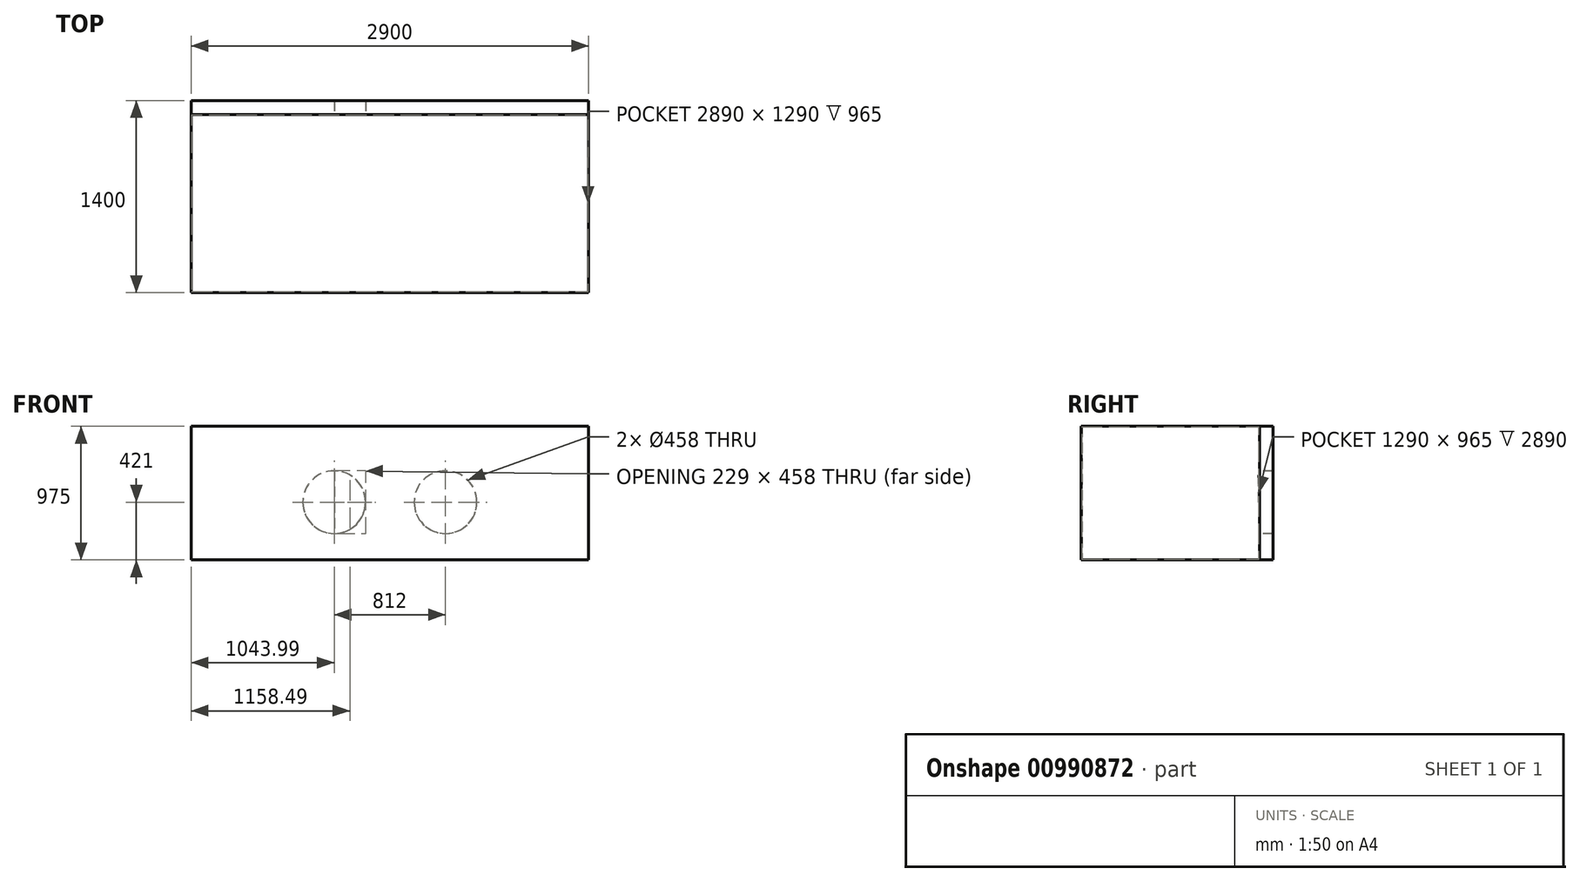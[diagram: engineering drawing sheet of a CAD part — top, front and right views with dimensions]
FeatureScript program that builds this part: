
annotation { "Feature Type Name" : "Feature", "Feature Type Description" : "" }
export const myFeature = defineFeature(function(context is Context, id is Id, definition is map)
    precondition{}
    {
        {
            var Q0;
            Q0=qCreatedBy(makeId("Top.planeOp"),FACE);
            var sketch = newSketch(context, id + "F0", { "sketchPlane" : qUnion([Q0])});
            skLineSegment(sketch, "E0", {"start": v(-44.36, 1284.12) * mm, "end": v(-44.36, -15.88) * mm});
            skLineSegment(sketch, "E1", {"start": v(-44.36, -15.88) * mm, "end": v(2855.64, -15.88) * mm});
            skLineSegment(sketch, "E2", {"start": v(2855.64, -15.88) * mm, "end": v(2855.64, 1284.12) * mm});
            skLineSegment(sketch, "E3", {"start": v(2855.64, 1284.12) * mm, "end": v(-44.36, 1284.12) * mm});
            skSolve(sketch);
        }
        {
            var Q0;
            Q0=makeQuery(id+"F0.imprint","IMPRINT",FACE,{"disambiguationData":[TD([[makeQuery(id+"F0.imprint","IMPRINT",EDGE,{"derivedFrom":sQuery(id+"F0.wireOp",EDGE,"E0")}),1.0]])]});
            extrude(context, id + "F1", {"entities" : qUnion([Q0]), "depth" : 975 * mm, "offsetDistance" : 25 * mm});
        }
        {
            var Q0;
            Q0=makeQuery(id+"F1.opExtrude","SWEPT_FACE",FACE,{"disambiguationData":[OSD([sQuery(id+"F0.wireOp",EDGE,"E3")])]});
            var Q1;
            Q1=makeQuery(id+"F1.opExtrude","SWEPT_BODY",BODY,{"disambiguationData":[OSD([sQuery(id+"F0.wireOp",EDGE,"E0"),sQuery(id+"F0.wireOp",EDGE,"E1"),sQuery(id+"F0.wireOp",EDGE,"E2"),sQuery(id+"F0.wireOp",EDGE,"E3")])]});
            shell(context, id + "F2", {"isHollow" : true, "entities" : qUnion([Q0]), "parts" : qUnion([Q1]), "thickness" : 5 * mm});
        }
        {
            var Q0;
            Q0=makeQuery(id+"F1.opExtrude","SWEPT_FACE",FACE,{"disambiguationData":[OSD([sQuery(id+"F0.wireOp",EDGE,"E3")])]});
            var sketch = newSketch(context, id + "F3", { "sketchPlane" : qUnion([Q0])});
            skLineSegment(sketch, "E4.0", {"start": v(-2855.64, 421) * mm, "end": v(44.36, 421) * mm});
            skLineSegment(sketch, "E5.0", {"start": v(-1811.64, 144.5) * mm, "end": v(-1811.64, 832.46) * mm});
            skLineSegment(sketch, "E6.0", {"start": v(-999.64, 910.53) * mm, "end": v(-999.64, 120.1) * mm});
            skCircle(sketch, "E7", {"center": v(-1811.64, 421) * mm, "radius": 229 * mm});
            skCircle(sketch, "E8", {"center": v(-999.64, 421) * mm, "radius": 229 * mm});
            skSolve(sketch);
        }
        {
            var Q0;
            {var subQ0=sQuery(id+"F3.wireOp",EDGE,"E7");var subQ1=sQuery(id+"F3.wireOp",EDGE,"E4.0");var subQ2=makeQuery(id+"F3.imprint","INTERSECT",VERTEX,{"disambiguationData":[OD(0.0)],"derivedFrom":[subQ1,subQ0]});Q0=makeQuery(id+"F3.imprint","IMPRINT",FACE,{"disambiguationData":[TD([[makeQuery(id+"F3.imprint","IMPRINT",EDGE,{"disambiguationData":[TD([[subQ2,-1.0]])],"derivedFrom":subQ1}),-1.0]])]});}
            var Q1;
            {var subQ0=sQuery(id+"F3.wireOp",EDGE,"E7");var subQ1=sQuery(id+"F3.wireOp",EDGE,"E4.0");var subQ2=makeQuery(id+"F3.imprint","INTERSECT",VERTEX,{"disambiguationData":[OD(0.0)],"derivedFrom":[subQ1,subQ0]});Q1=makeQuery(id+"F3.imprint","IMPRINT",FACE,{"disambiguationData":[TD([[makeQuery(id+"F3.imprint","IMPRINT",EDGE,{"disambiguationData":[TD([[subQ2,-1.0]])],"derivedFrom":subQ1}),1.0]])]});}
            var Q2;
            {var subQ0=sQuery(id+"F3.wireOp",EDGE,"E5.0");var subQ1=sQuery(id+"F3.wireOp",EDGE,"E4.0");var subQ2=makeQuery(id+"F3.imprint","INTERSECT",VERTEX,{"derivedFrom":[subQ1,subQ0]});Q2=makeQuery(id+"F3.imprint","IMPRINT",FACE,{"disambiguationData":[TD([[makeQuery(id+"F3.imprint","IMPRINT",EDGE,{"disambiguationData":[TD([[subQ2,-1.0]])],"derivedFrom":subQ1}),1.0]])]});}
            var Q3;
            {var subQ0=sQuery(id+"F3.wireOp",EDGE,"E5.0");var subQ1=sQuery(id+"F3.wireOp",EDGE,"E4.0");var subQ2=makeQuery(id+"F3.imprint","INTERSECT",VERTEX,{"derivedFrom":[subQ1,subQ0]});Q3=makeQuery(id+"F3.imprint","IMPRINT",FACE,{"disambiguationData":[TD([[makeQuery(id+"F3.imprint","IMPRINT",EDGE,{"disambiguationData":[TD([[subQ2,-1.0]])],"derivedFrom":subQ1}),-1.0]])]});}
            var Q4;
            {var subQ0=sQuery(id+"F3.wireOp",EDGE,"E8");var subQ1=sQuery(id+"F3.wireOp",EDGE,"E4.0");var subQ2=makeQuery(id+"F3.imprint","INTERSECT",VERTEX,{"disambiguationData":[OD(0.0)],"derivedFrom":[subQ1,subQ0]});Q4=makeQuery(id+"F3.imprint","IMPRINT",FACE,{"disambiguationData":[TD([[makeQuery(id+"F3.imprint","IMPRINT",EDGE,{"disambiguationData":[TD([[subQ2,-1.0]])],"derivedFrom":subQ1}),-1.0]])]});}
            var Q5;
            {var subQ0=sQuery(id+"F3.wireOp",EDGE,"E8");var subQ1=sQuery(id+"F3.wireOp",EDGE,"E4.0");var subQ2=makeQuery(id+"F3.imprint","INTERSECT",VERTEX,{"disambiguationData":[OD(0.0)],"derivedFrom":[subQ1,subQ0]});Q5=makeQuery(id+"F3.imprint","IMPRINT",FACE,{"disambiguationData":[TD([[makeQuery(id+"F3.imprint","IMPRINT",EDGE,{"disambiguationData":[TD([[subQ2,-1.0]])],"derivedFrom":subQ1}),1.0]])]});}
            var Q6;
            {var subQ0=sQuery(id+"F3.wireOp",EDGE,"E6.0");var subQ1=sQuery(id+"F3.wireOp",EDGE,"E4.0");var subQ2=makeQuery(id+"F3.imprint","INTERSECT",VERTEX,{"derivedFrom":[subQ1,subQ0]});Q6=makeQuery(id+"F3.imprint","IMPRINT",FACE,{"disambiguationData":[TD([[makeQuery(id+"F3.imprint","IMPRINT",EDGE,{"disambiguationData":[TD([[subQ2,-1.0]])],"derivedFrom":subQ1}),1.0]])]});}
            var Q7;
            {var subQ0=sQuery(id+"F3.wireOp",EDGE,"E6.0");var subQ1=sQuery(id+"F3.wireOp",EDGE,"E4.0");var subQ2=makeQuery(id+"F3.imprint","INTERSECT",VERTEX,{"derivedFrom":[subQ1,subQ0]});Q7=makeQuery(id+"F3.imprint","IMPRINT",FACE,{"disambiguationData":[TD([[makeQuery(id+"F3.imprint","IMPRINT",EDGE,{"disambiguationData":[TD([[subQ2,-1.0]])],"derivedFrom":subQ1}),-1.0]])]});}
            extrude(context, id + "F4", {"entities" : qUnion([Q0, Q1, Q2, Q3, Q4, Q5, Q6, Q7]), "depth" : 100 * mm, "offsetDistance" : 25 * mm});
        }
        {
            var Q0;
            Q0 = qSketchRegion(id + "F3", true);
            extrude(context, id + "F5", {"entities" : qUnion([Q0]), "operationType" : NewBodyOperationType.REMOVE, "oppositeDirection" : true, "depth" : 326 * mm, "offsetDistance" : 25 * mm});
        }
    });
